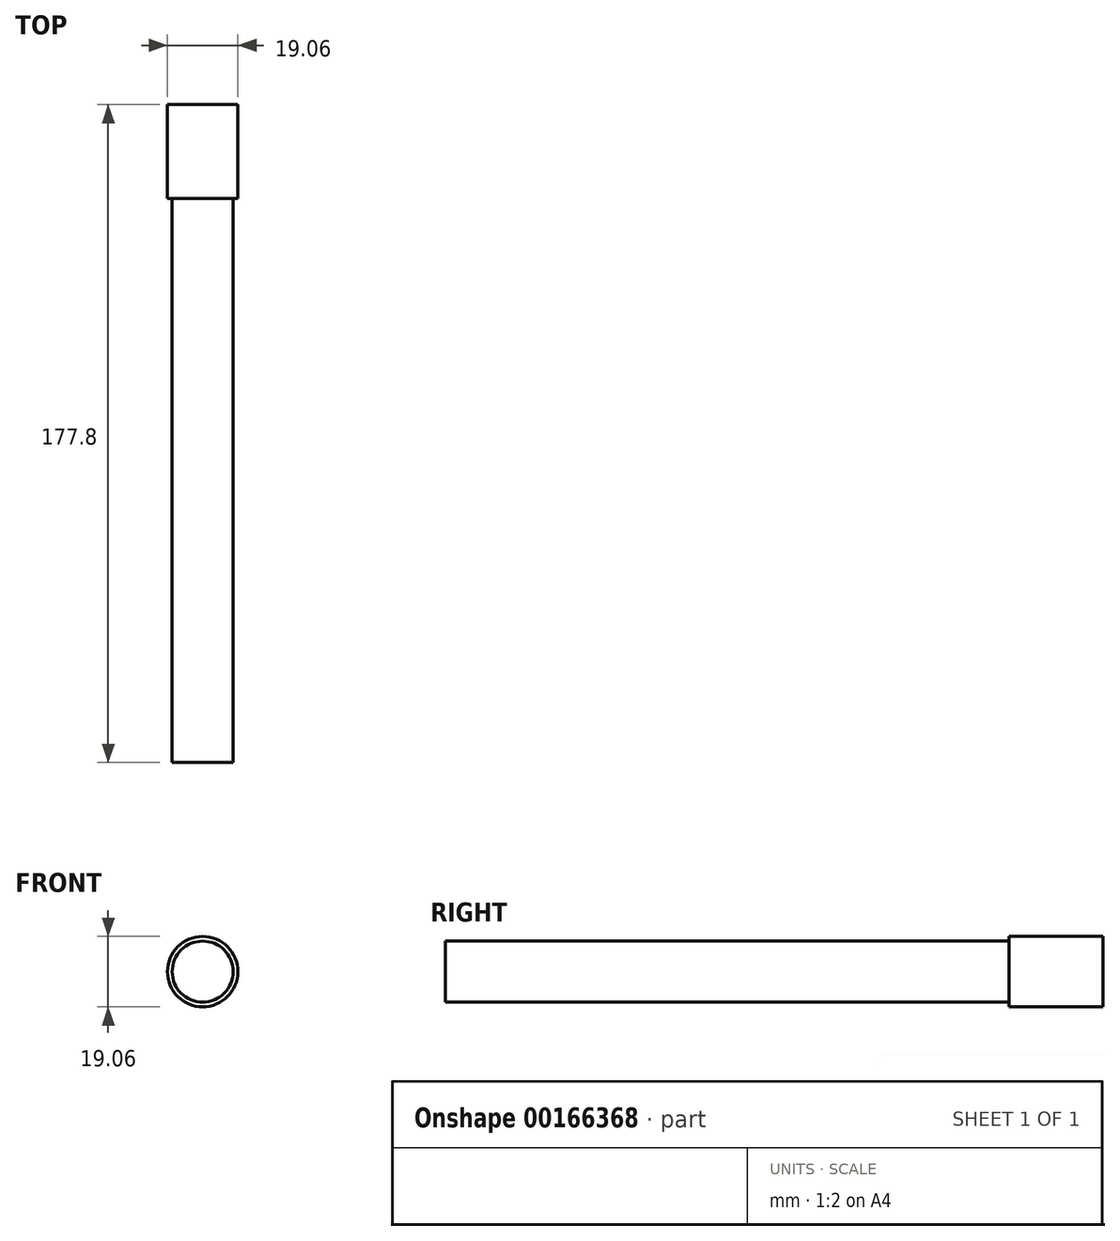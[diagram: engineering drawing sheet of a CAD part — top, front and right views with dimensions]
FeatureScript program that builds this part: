
annotation { "Feature Type Name" : "Feature", "Feature Type Description" : "" }
export const myFeature = defineFeature(function(context is Context, id is Id, definition is map)
    precondition{}
    {
        {
            var Q0;
            Q0=qCreatedBy(makeId("Front.planeOp"),FACE);
            var sketch = newSketch(context, id + "F0", { "sketchPlane" : qUnion([Q0])});
            skCircle(sketch, "E0", {"center": v(0, 0) * mm, "radius": 8.26 * mm});
            skSolve(sketch);
        }
        {
            var Q0;
            Q0=qCreatedBy(makeId("Front.planeOp"),FACE);
            var sketch = newSketch(context, id + "F1", { "sketchPlane" : qUnion([Q0])});
            skCircle(sketch, "E1", {"center": v(0, 0) * mm, "radius": 9.53 * mm});
            skSolve(sketch);
        }
        {
            var Q0;
            Q0 = qSketchRegion(id + "F0", true);
            extrude(context, id + "F2", {"entities" : qUnion([Q0]), "depth" : 177.8 * mm});
        }
        {
            var Q0;
            Q0 = qSketchRegion(id + "F1", true);
            extrude(context, id + "F3", {"entities" : qUnion([Q0]), "operationType" : NewBodyOperationType.ADD, "depth" : 25.4 * mm});
        }
    });
